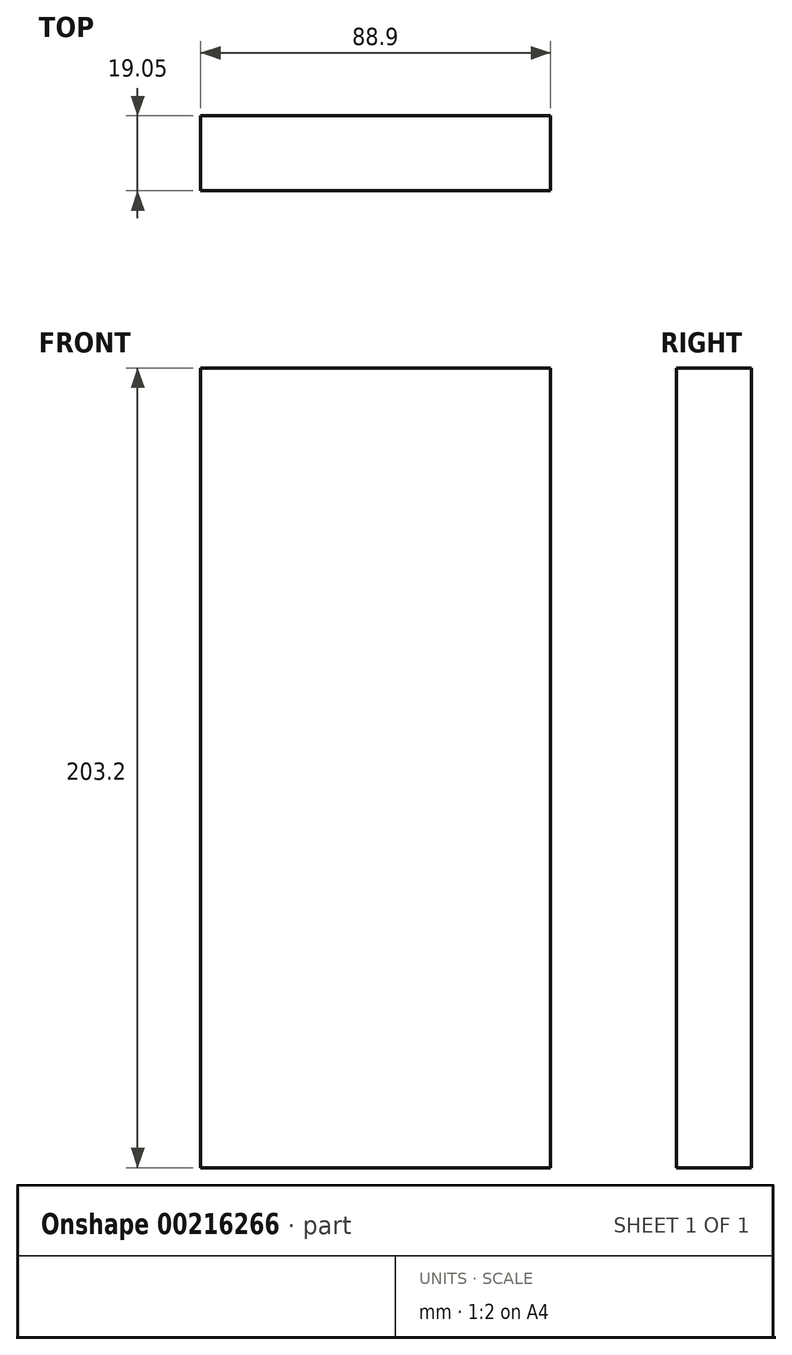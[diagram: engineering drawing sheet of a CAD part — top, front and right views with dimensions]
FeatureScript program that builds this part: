
annotation { "Feature Type Name" : "Feature", "Feature Type Description" : "" }
export const myFeature = defineFeature(function(context is Context, id is Id, definition is map)
    precondition{}
    {
        {
            var Q0;
            Q0=qCreatedBy(makeId("Front.planeOp"),FACE);
            var sketch = newSketch(context, id + "F0", { "sketchPlane" : qUnion([Q0])});
            skLineSegment(sketch, "E0", {"start": v(-1661.52, -1606) * mm, "end": v(-1572.62, -1606) * mm});
            skLineSegment(sketch, "E1", {"start": v(-1572.62, -1606) * mm, "end": v(-1572.62, -1402.8) * mm});
            skLineSegment(sketch, "E2", {"start": v(-1572.62, -1402.8) * mm, "end": v(-1661.52, -1402.8) * mm});
            skLineSegment(sketch, "E3", {"start": v(-1661.52, -1402.8) * mm, "end": v(-1661.52, -1606) * mm});
            skSolve(sketch);
        }
        {
            var Q0;
            Q0=makeQuery(id+"F0.imprint","IMPRINT",FACE,{"disambiguationData":[TD([[makeQuery(id+"F0.imprint","IMPRINT",EDGE,{"derivedFrom":sQuery(id+"F0.wireOp",EDGE,"E0")}),1.0]])]});
            extrude(context, id + "F1", {"entities" : qUnion([Q0]), "depth" : 19.05 * mm});
        }
    });
